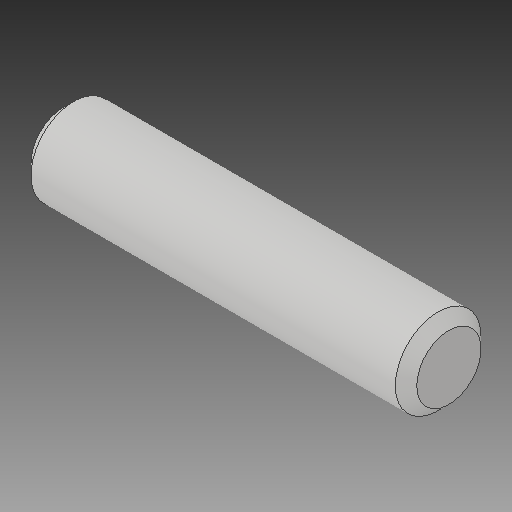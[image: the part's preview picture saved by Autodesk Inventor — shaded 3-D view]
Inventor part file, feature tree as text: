
AUTODESK INVENTOR PART (.ipt)
format: ipt  version: 2017 (Build 210142000, 142)  size: 86,528 bytes
history: native  units: in
note: dims shown in document units (in); Inventor stores cm internally (conversion verified against a paired STEP export)
features: chamfer x1
ambient origin geometry x8: Origin, YZ Plane, XZ Plane, XY Plane, X Axis, Y Axis, Z Axis, Center Point
bodies: Solid1 (feature_tree)
feature tree (1):
  chamfer  "Chamfer1"  [1 undecoded]
note: 1 required parameter value undecoded (feature->parameter linkage not recoverable at this tier; creation-order binding heuristic only, values carry confidence <= 0.55)
